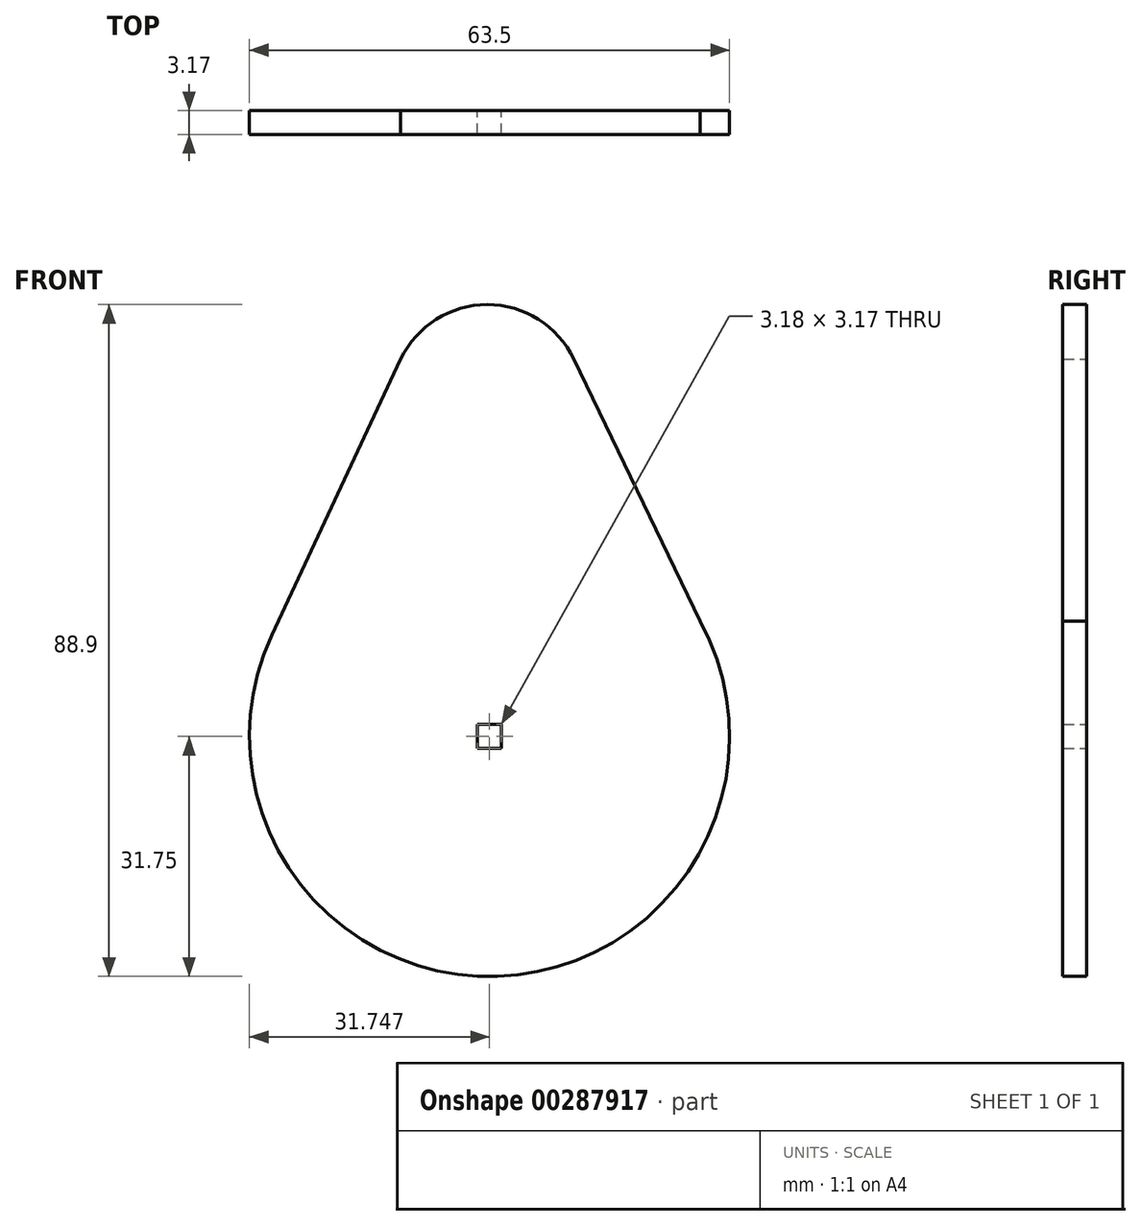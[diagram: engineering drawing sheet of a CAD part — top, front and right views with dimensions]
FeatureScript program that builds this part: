
annotation { "Feature Type Name" : "Feature", "Feature Type Description" : "" }
export const myFeature = defineFeature(function(context is Context, id is Id, definition is map)
    precondition{}
    {
        {
            var Q0;
            Q0=qCreatedBy(makeId("Front.planeOp"),FACE);
            var sketch = newSketch(context, id + "F0", { "sketchPlane" : qUnion([Q0])});
            skLineSegment(sketch, "E0.bottom", {"start": v(-46.77, 30.3) * mm, "end": v(-43.6, 30.3) * mm});
            skLineSegment(sketch, "E0.top", {"start": v(-46.77, 27.13) * mm, "end": v(-43.6, 27.13) * mm});
            skLineSegment(sketch, "E0.left", {"start": v(-46.77, 30.3) * mm, "end": v(-46.77, 27.13) * mm});
            skLineSegment(sketch, "E0.right", {"start": v(-43.6, 30.3) * mm, "end": v(-43.6, 27.13) * mm});
            skCircle(sketch, "E1", {"center": v(-45.18, 28.72) * mm, "radius": 31.75 * mm});
            skPoint(sketch, "E1.centerSnap0", {"position": v(-45.18, 30.3) * mm});
            skPoint(sketch, "E1.centerSnap1", {"position": v(-43.6, 28.72) * mm});
            skCircle(sketch, "E2", {"center": v(-45.49, 73.17) * mm, "radius": 12.7 * mm});
            skLineSegment(sketch, "E3", {"start": v(-17.36, 44) * mm, "end": v(-34.04, 78.68) * mm});
            skLineSegment(sketch, "E4", {"start": v(-34.04, 78.68) * mm, "end": v(-56.93, 78.68) * mm});
            skLineSegment(sketch, "E5", {"start": v(-56.93, 78.68) * mm, "end": v(-73.96, 42.13) * mm});
            skSolve(sketch);
        }
        {
            var Q0;
            Q0=makeQuery(id+"F0.imprint","IMPRINT",FACE,{"disambiguationData":[TD([[makeQuery(id+"F0.imprint","IMPRINT",EDGE,{"derivedFrom":sQuery(id+"F0.wireOp",EDGE,"E0.bottom")}),1.0]])]});
            var Q1;
            {var subQ0=sQuery(id+"F0.wireOp",EDGE,"E3");Q1=makeQuery(id+"F0.imprint","IMPRINT",FACE,{"disambiguationData":[TD([[makeQuery(id+"F0.imprint","IMPRINT",EDGE,{"derivedFrom":subQ0}),1.0]])]});}
            var Q2;
            {var subQ0=sQuery(id+"F0.wireOp",EDGE,"E4");Q2=makeQuery(id+"F0.imprint","IMPRINT",FACE,{"disambiguationData":[TD([[makeQuery(id+"F0.imprint","IMPRINT",EDGE,{"derivedFrom":subQ0}),1.0]])]});}
            var Q3;
            {var subQ0=sQuery(id+"F0.wireOp",EDGE,"E4");Q3=makeQuery(id+"F0.imprint","IMPRINT",FACE,{"disambiguationData":[TD([[makeQuery(id+"F0.imprint","IMPRINT",EDGE,{"derivedFrom":subQ0}),-1.0]])]});}
            extrude(context, id + "F1", {"entities" : qUnion([Q0, Q1, Q2, Q3]), "depth" : 3.17 * mm});
        }
    });
